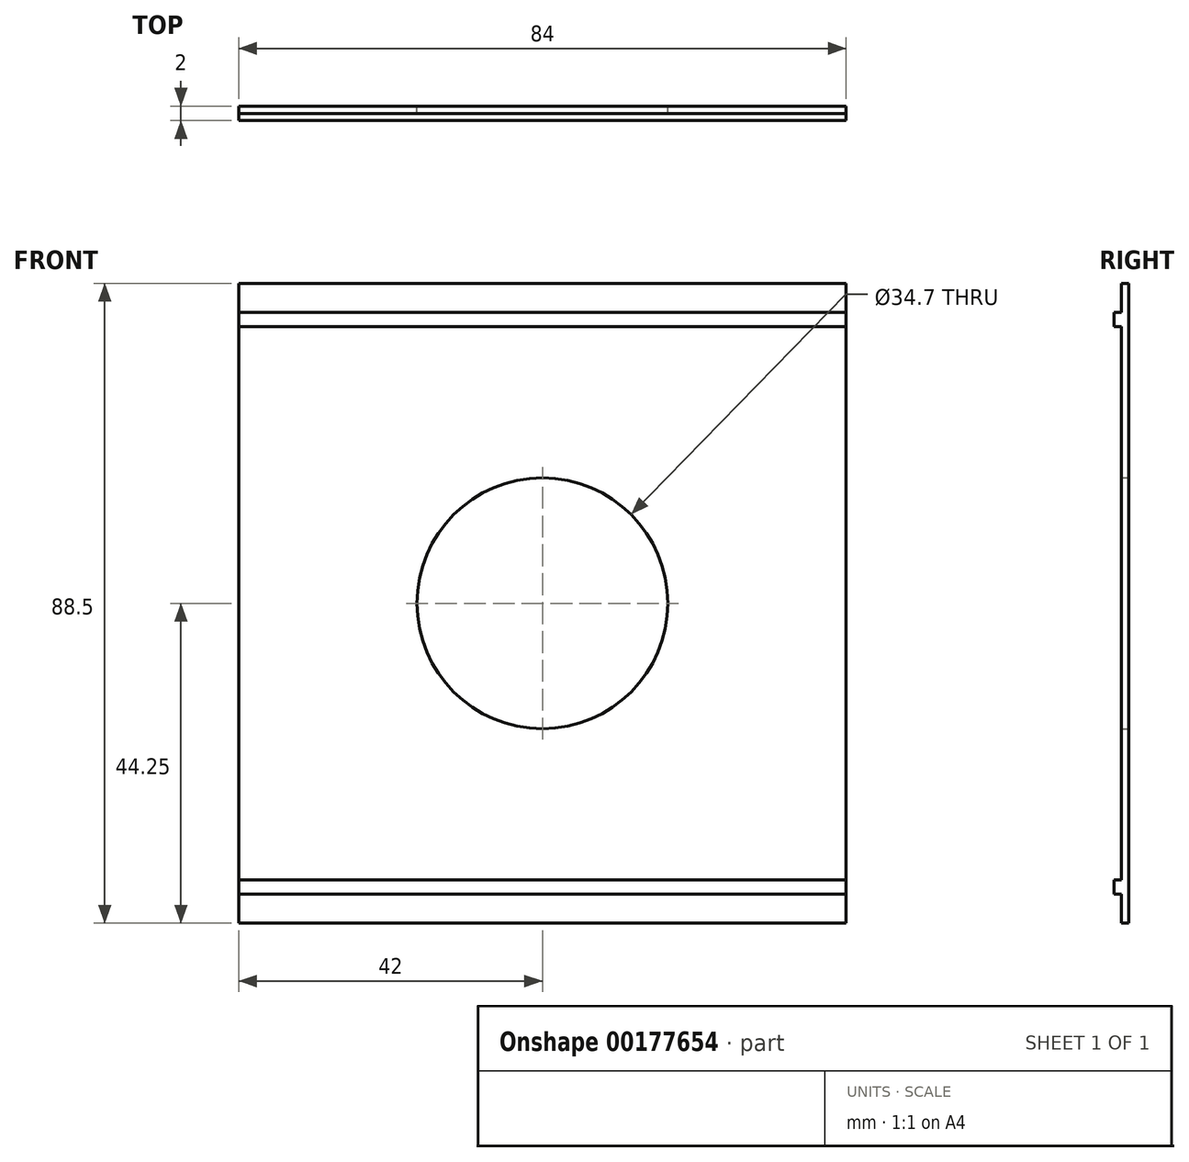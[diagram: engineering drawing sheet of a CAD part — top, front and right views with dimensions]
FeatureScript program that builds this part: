
annotation { "Feature Type Name" : "Feature", "Feature Type Description" : "" }
export const myFeature = defineFeature(function(context is Context, id is Id, definition is map)
    precondition{}
    {
        {
            var Q0;
            Q0=qCreatedBy(makeId("Front.planeOp"),FACE);
            var sketch = newSketch(context, id + "F0", { "sketchPlane" : qUnion([Q0])});
            skLineSegment(sketch, "E0.bottom", {"start": v(42, 44.25) * mm, "end": v(-42, 44.25) * mm});
            skLineSegment(sketch, "E0.top", {"start": v(42, -44.25) * mm, "end": v(-42, -44.25) * mm});
            skLineSegment(sketch, "E0.left", {"start": v(42, 44.25) * mm, "end": v(42, -44.25) * mm});
            skLineSegment(sketch, "E0.right", {"start": v(-42, 44.25) * mm, "end": v(-42, -44.25) * mm});
            skPoint(sketch, "E0.middle", {"position": v(0, 0) * mm});
            skCircle(sketch, "E1", {"center": v(0, 0) * mm, "radius": 17.35 * mm});
            skSolve(sketch);
        }
        {
            var Q0;
            Q0 = qSketchRegion(id + "F0", true);
            extrude(context, id + "F1", {"entities" : qUnion([Q0]), "depth" : 1 * mm});
        }
        {
            var Q0;
            Q0=makeQuery(id+"F1.opExtrude","CAP_FACE",FACE,{"disambiguationData":[OSD([sQuery(id+"F0.wireOp",EDGE,"E0.bottom"),sQuery(id+"F0.wireOp",EDGE,"E0.top"),sQuery(id+"F0.wireOp",EDGE,"E0.left"),sQuery(id+"F0.wireOp",EDGE,"E0.right"),sQuery(id+"F0.wireOp",EDGE,"E1")])],"isStart":false});
            var sketch = newSketch(context, id + "F2", { "sketchPlane" : qUnion([Q0])});
            skLineSegment(sketch, "E2.bottom", {"start": v(-42, 40.25) * mm, "end": v(42, 40.25) * mm});
            skLineSegment(sketch, "E2.top", {"start": v(-42, 38.25) * mm, "end": v(42, 38.25) * mm});
            skLineSegment(sketch, "E2.left", {"start": v(-42, 40.25) * mm, "end": v(-42, 38.25) * mm});
            skLineSegment(sketch, "E2.right", {"start": v(42, 40.25) * mm, "end": v(42, 38.25) * mm});
            skLineSegment(sketch, "E3.bottom", {"start": v(-42, -38.25) * mm, "end": v(42, -38.25) * mm});
            skLineSegment(sketch, "E3.top", {"start": v(-42, -40.25) * mm, "end": v(42, -40.25) * mm});
            skLineSegment(sketch, "E3.left", {"start": v(-42, -38.25) * mm, "end": v(-42, -40.25) * mm});
            skLineSegment(sketch, "E3.right", {"start": v(42, -38.25) * mm, "end": v(42, -40.25) * mm});
            skSolve(sketch);
        }
        {
            var Q0;
            Q0 = qSketchRegion(id + "F2", true);
            extrude(context, id + "F3", {"entities" : qUnion([Q0]), "operationType" : NewBodyOperationType.ADD, "depth" : 1 * mm});
        }
    });
